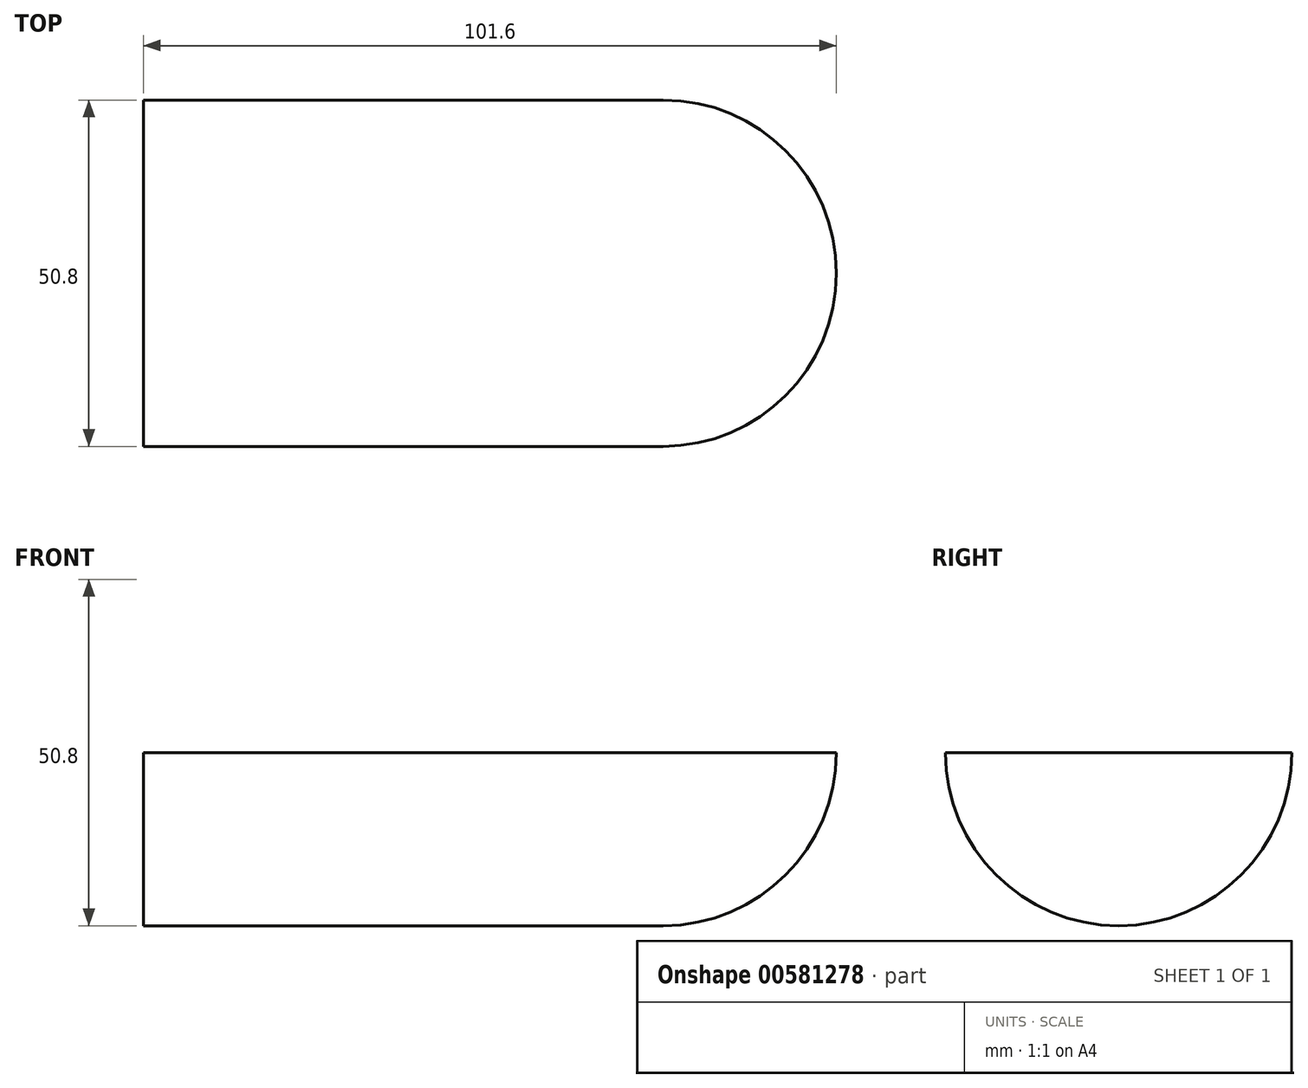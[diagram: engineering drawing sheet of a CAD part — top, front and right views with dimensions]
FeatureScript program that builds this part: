
annotation { "Feature Type Name" : "Feature", "Feature Type Description" : "" }
export const myFeature = defineFeature(function(context is Context, id is Id, definition is map)
    precondition{}
    {
        {
            var Q0;
            Q0=qCreatedBy(makeId("Front.planeOp"),FACE);
            var sketch = newSketch(context, id + "F0", { "sketchPlane" : qUnion([Q0])});
            skLineSegment(sketch, "E0.bottom", {"start": v(-17, -5.14) * mm, "end": v(59.2, -5.14) * mm});
            skLineSegment(sketch, "E0.top", {"start": v(-17, -30.54) * mm, "end": v(59.2, -30.54) * mm});
            skLineSegment(sketch, "E0.left", {"start": v(-17, -5.14) * mm, "end": v(-17, -30.54) * mm});
            skLineSegment(sketch, "E0.right", {"start": v(59.2, -5.14) * mm, "end": v(59.2, -30.54) * mm});
            skLineSegment(sketch, "E1", {"start": v(59.2, -5.14) * mm, "end": v(84.6, -5.14) * mm});
            skArc(sketch, "E2", {"start": v(59.2, -30.54) * mm, "mid": v(77.16, -23.1) * mm, "end": v(84.6, -5.14) * mm});
            skSolve(sketch);
        }
        {
            var Q0;
            Q0=qSketchRegion(id+"F0",true);
            extrude(context, id + "F1", {"entities" : qUnion([Q0]), "depth" : 50.8 * mm, "offsetDistance" : 25.4 * mm});
        }
        {
            var Q0;
            Q0=makeQuery(id+"F1.opExtrude","CAP_EDGE",EDGE,{"disambiguationData":[OSD([sQuery(id+"F0.wireOp",EDGE,"E0.top")])],"isStart":false});
            fillet(context, id + "F2", {"entities" : qUnion([Q0]), "radius" : 25.4 * mm, "tangentPropagation" : true, "allowEdgeOverflow" : false});
        }
        {
            var Q0;
            Q0=makeQuery(id+"F1.opExtrude","CAP_EDGE",EDGE,{"disambiguationData":[OSD([sQuery(id+"F0.wireOp",EDGE,"E0.top")])],"isStart":true});
            fillet(context, id + "F3", {"entities" : qUnion([Q0]), "radius" : 25.4 * mm, "tangentPropagation" : true, "allowEdgeOverflow" : false});
        }
    });
